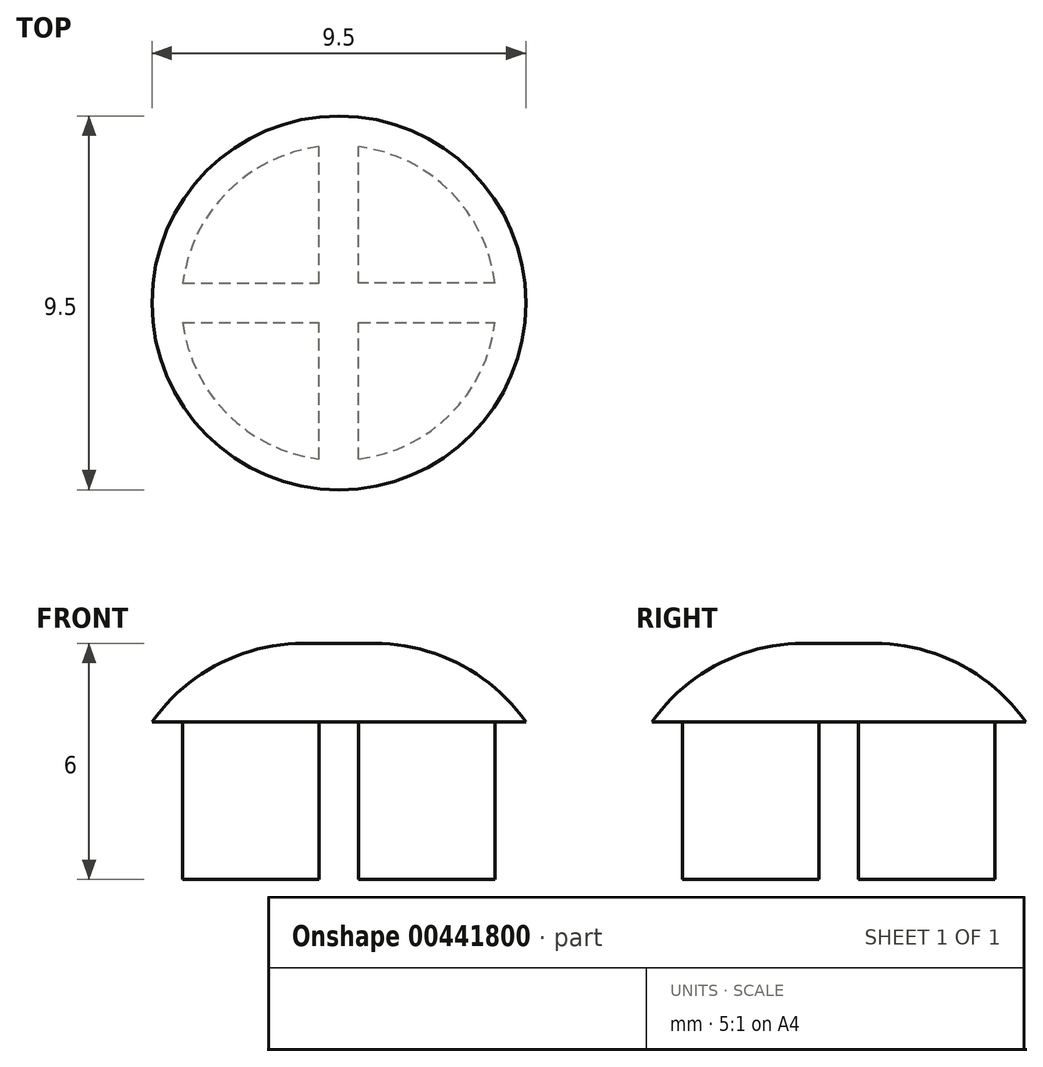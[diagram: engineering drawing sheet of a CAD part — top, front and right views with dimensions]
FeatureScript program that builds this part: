
annotation { "Feature Type Name" : "Feature", "Feature Type Description" : "" }
export const myFeature = defineFeature(function(context is Context, id is Id, definition is map)
    precondition{}
    {
        {
            var Q0;
            Q0=qCreatedBy(makeId("Top.planeOp"),FACE);
            var sketch = newSketch(context, id + "F0", { "sketchPlane" : qUnion([Q0])});
            skCircle(sketch, "E0", {"center": v(0, 0) * mm, "radius": 4.75 * mm});
            skArc(sketch, "E1", {"start": v(-3.97, -0.5) * mm, "mid": v(-2.83, -2.83) * mm, "end": v(-0.5, -3.97) * mm});
            skLineSegment(sketch, "E2", {"start": v(-3.97, -0.5) * mm, "end": v(-2.75, -0.5) * mm});
            skLineSegment(sketch, "E3", {"start": v(-3.97, 0.5) * mm, "end": v(-2.75, 0.5) * mm});
            skLineSegment(sketch, "E4.trimOffspring", {"start": v(2.75, -0.5) * mm, "end": v(3.97, -0.5) * mm});
            skLineSegment(sketch, "E5.trimOffspring", {"start": v(2.75, 0.5) * mm, "end": v(3.97, 0.5) * mm});
            skArc(sketch, "E6.trimOffspring", {"start": v(3.97, 0.5) * mm, "mid": v(2.83, 2.83) * mm, "end": v(0.5, 3.97) * mm});
            skLineSegment(sketch, "E7", {"start": v(-0.5, -3.97) * mm, "end": v(-0.5, -2.75) * mm});
            skLineSegment(sketch, "E8", {"start": v(0.5, -3.97) * mm, "end": v(0.5, -2.75) * mm});
            skArc(sketch, "E9.trimOffspring", {"start": v(0.5, -3.97) * mm, "mid": v(2.83, -2.83) * mm, "end": v(3.97, -0.5) * mm});
            skLineSegment(sketch, "E10.trimOffspring", {"start": v(-0.5, 2.75) * mm, "end": v(-0.5, 3.97) * mm});
            skLineSegment(sketch, "E11.trimOffspring", {"start": v(0.5, 2.75) * mm, "end": v(0.5, 3.97) * mm});
            skArc(sketch, "E12.trimOffspring", {"start": v(-0.5, 3.97) * mm, "mid": v(-2.83, 2.83) * mm, "end": v(-3.97, 0.5) * mm});
            skLineSegment(sketch, "E13", {"start": v(0.5, -2.75) * mm, "end": v(0.5, -0.5) * mm});
            skLineSegment(sketch, "E14", {"start": v(0.5, -0.5) * mm, "end": v(2.75, -0.5) * mm});
            skLineSegment(sketch, "E15", {"start": v(2.75, 0.5) * mm, "end": v(0.5, 0.5) * mm});
            skLineSegment(sketch, "E16", {"start": v(0.5, 0.5) * mm, "end": v(0.5, 2.75) * mm});
            skLineSegment(sketch, "E17", {"start": v(-0.5, 2.75) * mm, "end": v(-0.5, 0.5) * mm});
            skLineSegment(sketch, "E18", {"start": v(-0.5, 0.5) * mm, "end": v(-2.75, 0.5) * mm});
            skLineSegment(sketch, "E19", {"start": v(-2.75, -0.5) * mm, "end": v(-0.5, -0.5) * mm});
            skLineSegment(sketch, "E20", {"start": v(-0.5, -0.5) * mm, "end": v(-0.5, -2.75) * mm});
            skSolve(sketch);
        }
        {
            var Q0;
            Q0=makeQuery(id+"F0.imprint","IMPRINT",FACE,{"disambiguationData":[TD([[makeQuery(id+"F0.imprint","IMPRINT",EDGE,{"derivedFrom":sQuery(id+"F0.wireOp",EDGE,"E0")}),1.0]])]});
            var Q1;
            Q1=makeQuery(id+"F0.imprint","IMPRINT",FACE,{"disambiguationData":[TD([[makeQuery(id+"F0.imprint","IMPRINT",EDGE,{"derivedFrom":sQuery(id+"F0.wireOp",EDGE,"7o0uFvpW-uGEu-TaPo-yNOh-SOGGR3qKdKIB")}),1.0]])]});
            var Q2;
            Q2=makeQuery(id+"F0.imprint","IMPRINT",FACE,{"disambiguationData":[TD([[makeQuery(id+"F0.imprint","IMPRINT",EDGE,{"derivedFrom":sQuery(id+"F0.wireOp",EDGE,"E1")}),1.0]])]});
            var Q3;
            Q3=makeQuery(id+"F0.imprint","IMPRINT",FACE,{"disambiguationData":[TD([[makeQuery(id+"F0.imprint","IMPRINT",EDGE,{"derivedFrom":sQuery(id+"F0.wireOp",EDGE,"E3")}),1.0]])]});
            var Q4;
            Q4=makeQuery(id+"F0.imprint","IMPRINT",FACE,{"disambiguationData":[TD([[makeQuery(id+"F0.imprint","IMPRINT",EDGE,{"derivedFrom":sQuery(id+"F0.wireOp",EDGE,"E5.trimOffspring")}),1.0]])]});
            var Q5;
            Q5=makeQuery(id+"F0.imprint","IMPRINT",FACE,{"disambiguationData":[TD([[makeQuery(id+"F0.imprint","IMPRINT",EDGE,{"derivedFrom":sQuery(id+"F0.wireOp",EDGE,"E4.trimOffspring")}),-1.0]])]});
            extrude(context, id + "F1", {"entities" : qUnion([Q0, Q1, Q2, Q3, Q4, Q5]), "depth" : 2 * mm});
        }
        {
            var Q0;
            Q0=makeQuery(id+"F0.imprint","IMPRINT",FACE,{"disambiguationData":[TD([[makeQuery(id+"F0.imprint","IMPRINT",EDGE,{"derivedFrom":sQuery(id+"F0.wireOp",EDGE,"E3")}),1.0]])]});
            var Q1;
            Q1=makeQuery(id+"F0.imprint","IMPRINT",FACE,{"disambiguationData":[TD([[makeQuery(id+"F0.imprint","IMPRINT",EDGE,{"derivedFrom":sQuery(id+"F0.wireOp",EDGE,"E1")}),1.0]])]});
            var Q2;
            Q2=makeQuery(id+"F0.imprint","IMPRINT",FACE,{"disambiguationData":[TD([[makeQuery(id+"F0.imprint","IMPRINT",EDGE,{"derivedFrom":sQuery(id+"F0.wireOp",EDGE,"E4.trimOffspring")}),-1.0]])]});
            var Q3;
            Q3=makeQuery(id+"F0.imprint","IMPRINT",FACE,{"disambiguationData":[TD([[makeQuery(id+"F0.imprint","IMPRINT",EDGE,{"derivedFrom":sQuery(id+"F0.wireOp",EDGE,"E5.trimOffspring")}),1.0]])]});
            extrude(context, id + "F2", {"entities" : qUnion([Q0, Q1, Q2, Q3]), "operationType" : NewBodyOperationType.ADD, "oppositeDirection" : true, "depth" : 4 * mm});
        }
        {
            var Q0;
            Q0=makeQuery(id+"F1.opExtrude","CAP_EDGE",EDGE,{"disambiguationData":[OSD([sQuery(id+"F0.wireOp",EDGE,"E0")])],"isStart":false});
            fillet(context, id + "F3", {"entities" : qUnion([Q0]), "radius" : 4.7 * mm, "tangentPropagation" : true, "allowEdgeOverflow" : false});
        }
    });
